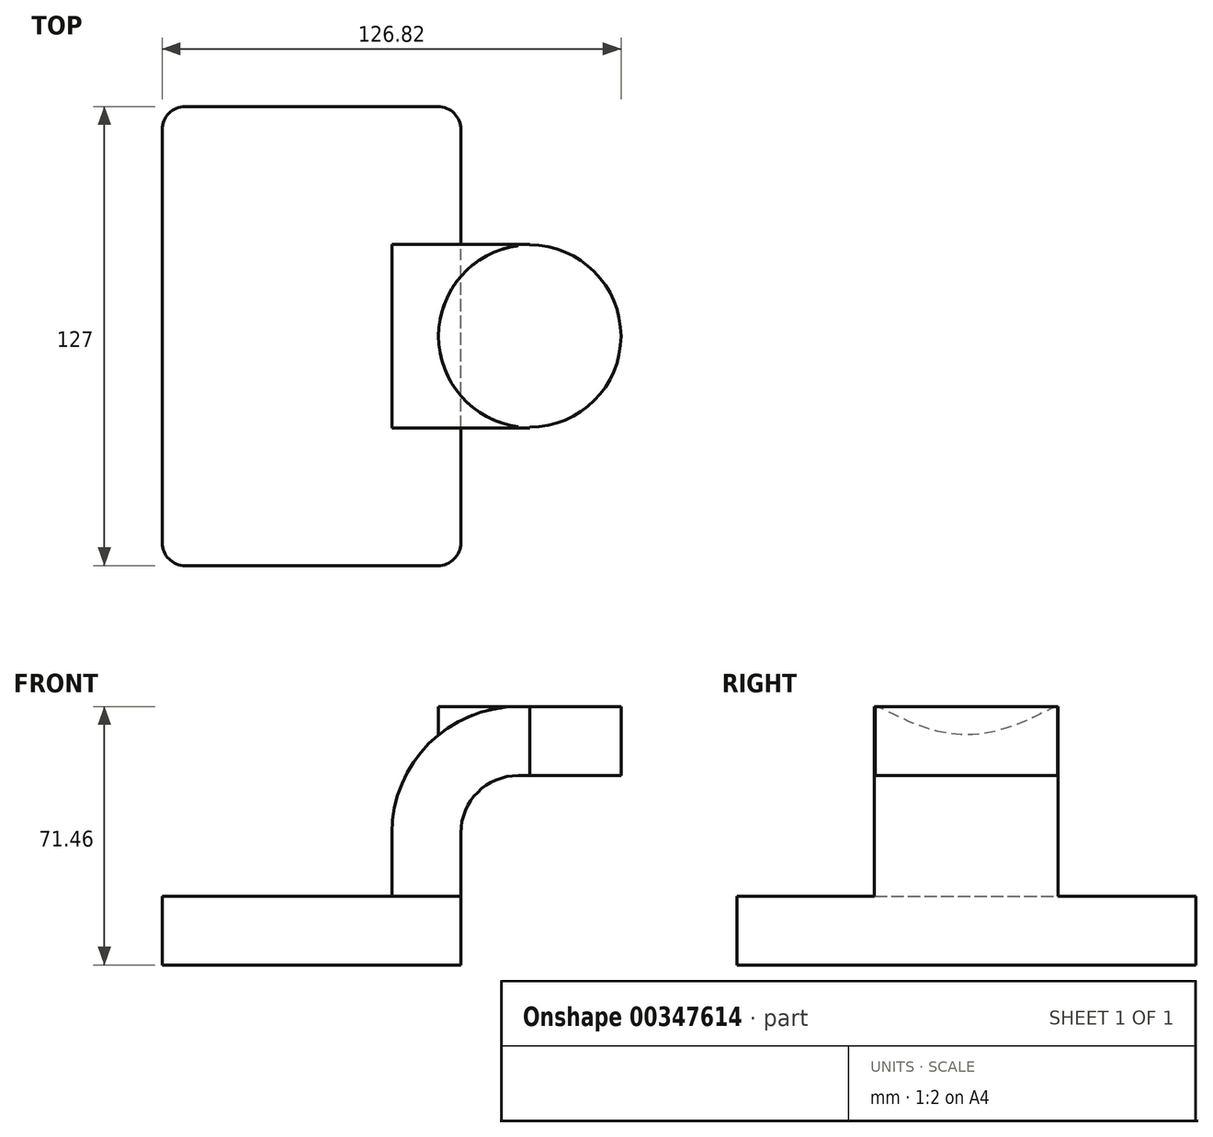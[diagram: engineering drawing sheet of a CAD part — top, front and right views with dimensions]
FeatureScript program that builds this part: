
annotation { "Feature Type Name" : "Feature", "Feature Type Description" : "" }
export const myFeature = defineFeature(function(context is Context, id is Id, definition is map)
    precondition{}
    {
        {
            var Q0;
            Q0=qCreatedBy(makeId("Front.planeOp"),FACE);
            var sketch = newSketch(context, id + "F0", { "sketchPlane" : qUnion([Q0])});
            skLineSegment(sketch, "E0.bottom", {"start": v(41.28, -9.52) * mm, "end": v(-41.28, -9.53) * mm});
            skLineSegment(sketch, "E0.top", {"start": v(41.28, 9.53) * mm, "end": v(-41.28, 9.53) * mm});
            skLineSegment(sketch, "E0.left", {"start": v(41.28, -9.52) * mm, "end": v(41.28, 9.53) * mm});
            skLineSegment(sketch, "E0.right", {"start": v(-41.28, -9.53) * mm, "end": v(-41.28, 9.53) * mm});
            skPoint(sketch, "E0.middle", {"position": v(0, 0) * mm});
            skLineSegment(sketch, "E1.bottom", {"start": v(111.12, 38.1) * mm, "end": v(60.32, 38.1) * mm});
            skLineSegment(sketch, "E1.top", {"start": v(111.12, 66.68) * mm, "end": v(60.32, 66.68) * mm});
            skLineSegment(sketch, "E1.left", {"start": v(111.12, 38.1) * mm, "end": v(111.12, 66.68) * mm});
            skLineSegment(sketch, "E1.right", {"start": v(60.32, 38.1) * mm, "end": v(60.32, 66.68) * mm});
            skPoint(sketch, "E1.middle", {"position": v(85.72, 52.39) * mm});
            skLineSegment(sketch, "E2", {"start": v(41.28, 9.53) * mm, "end": v(41.28, 27) * mm});
            skArc(sketch, "E3", {"start": v(41.27, 27) * mm, "mid": v(45.92, 38.23) * mm, "end": v(57.15, 42.88) * mm});
            skLineSegment(sketch, "E4", {"start": v(57.15, 42.88) * mm, "end": v(85.55, 42.88) * mm});
            skLineSegment(sketch, "E5.0", {"start": v(57.15, 61.93) * mm, "end": v(85.55, 61.93) * mm});
            skArc(sketch, "E5.1", {"start": v(22.22, 27) * mm, "mid": v(32.45, 51.7) * mm, "end": v(57.15, 61.93) * mm});
            skLineSegment(sketch, "E5.2", {"start": v(22.22, 9.53) * mm, "end": v(22.22, 27) * mm});
            skFitSpline(sketch, "E6", {"points": [v(193.47, -11.96) * mm, v(193.07, -11.64) * mm], "startDerivative": vector(-0.4, 0.32) * mm, "endDerivative": vector(-0.4, 0.32) * mm});
            skFitSpline(sketch, "E7", {"points": [v(-41.28, 9.53) * mm, v(57.15, 61.93) * mm], "startDerivative": vector(1.13, 74.72) * mm, "endDerivative": vector(171.45, 0) * mm});
            skLineSegment(sketch, "E8", {"start": v(85.55, 61.93) * mm, "end": v(85.55, 42.88) * mm});
            skSolve(sketch);
        }
        {
            var Q0;
            Q0=makeQuery(id+"F0.imprint","IMPRINT",FACE,{"disambiguationData":[TD([[makeQuery(id+"F0.imprint","IMPRINT",EDGE,{"derivedFrom":sQuery(id+"F0.wireOp",EDGE,"E0.bottom")}),-1.0]])]});
            extrude(context, id + "F1", {"entities" : qUnion([Q0]), "endBound" : BoundingType.SYMMETRIC, "depth" : 127 * mm});
        }
        {
            var Q0;
            {var subQ1=sQuery(id+"F0.wireOp",EDGE,"E2");Q0=makeQuery(id+"F0.imprint","IMPRINT",FACE,{"disambiguationData":[TD([[makeQuery(id+"F0.imprint","IMPRINT",EDGE,{"derivedFrom":subQ1}),1.0]])]});}
            extrude(context, id + "F2", {"entities" : qUnion([Q0]), "operationType" : NewBodyOperationType.ADD, "endBound" : BoundingType.SYMMETRIC, "depth" : 50.8 * mm});
        }
        {
            var Q0;
            Q0=makeQuery(id+"F0.imprint","IMPRINT",FACE,{"disambiguationData":[TD([[makeQuery(id+"F0.imprint","IMPRINT",EDGE,{"derivedFrom":sQuery(id+"F0.wireOp",EDGE,"E5.1")}),1.0]])]});
            extrude(context, id + "F3", {"entities" : qUnion([Q0]), "operationType" : NewBodyOperationType.ADD, "endBound" : BoundingType.SYMMETRIC, "depth" : 15.88 * mm});
        }
        {
            var Q0;
            {var subQ5=sQuery(id+"F0.wireOp",EDGE,"E8");Q0=makeQuery(id+"F0.imprint","IMPRINT",FACE,{"disambiguationData":[TD([[makeQuery(id+"F0.imprint","IMPRINT",EDGE,{"derivedFrom":subQ5}),-1.0]])]});}
            var Q1;
            Q1=sQuery(id+"F0.wireOp",EDGE,"E1.right");
            revolve(context, id + "F4", {"operationType" : NewBodyOperationType.ADD, "entities" : qUnion([Q0]), "axis" : qUnion([Q1]), "revolveType" : RevolveType.FULL});
        }
        {
            var Q0;
            Q0=makeQuery(id+"F1.opExtrude","CAP_EDGE",EDGE,{"disambiguationData":[OSD([sQuery(id+"F0.wireOp",EDGE,"E0.left")])],"isStart":false});
            var Q1;
            Q1=makeQuery(id+"F1.opExtrude","CAP_EDGE",EDGE,{"disambiguationData":[OSD([sQuery(id+"F0.wireOp",EDGE,"E0.right")])],"isStart":false});
            var Q2;
            Q2=makeQuery(id+"F1.opExtrude","CAP_EDGE",EDGE,{"disambiguationData":[OSD([sQuery(id+"F0.wireOp",EDGE,"E0.left")])],"isStart":true});
            var Q3;
            Q3=makeQuery(id+"F1.opExtrude","CAP_EDGE",EDGE,{"disambiguationData":[OSD([sQuery(id+"F0.wireOp",EDGE,"E0.right")])],"isStart":true});
            fillet(context, id + "F5", {"entities" : qUnion([Q0, Q1, Q2, Q3]), "radius" : 6.35 * mm, "tangentPropagation" : true, "allowEdgeOverflow" : false});
        }
    });
